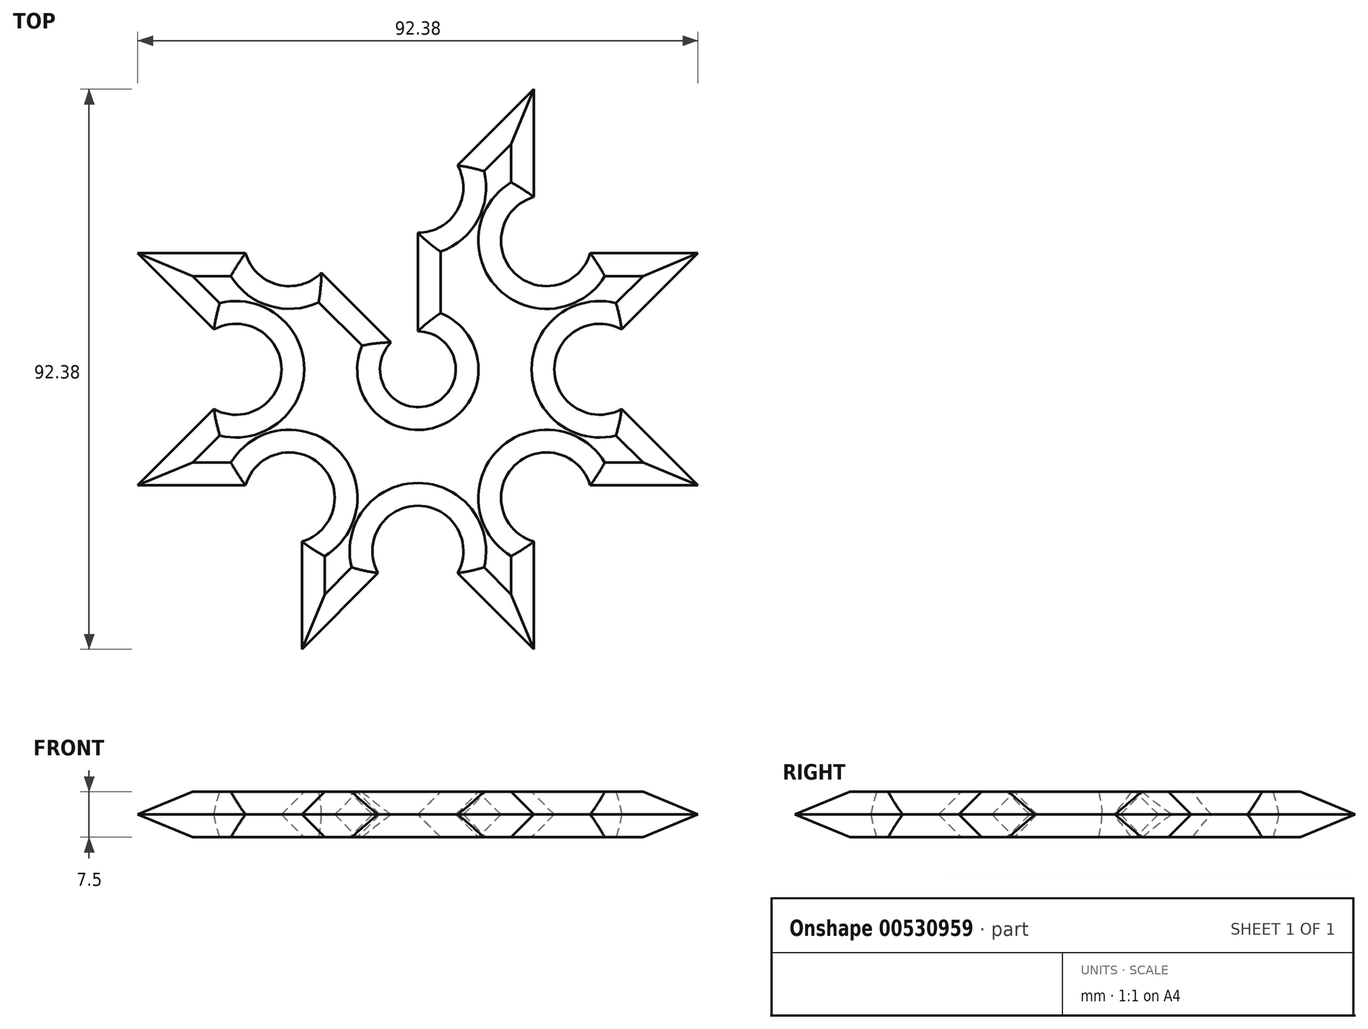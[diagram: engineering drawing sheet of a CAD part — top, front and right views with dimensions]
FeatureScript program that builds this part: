
annotation { "Feature Type Name" : "Feature", "Feature Type Description" : "" }
export const myFeature = defineFeature(function(context is Context, id is Id, definition is map)
    precondition{}
    {
        {
            var Q0;
            Q0=qCreatedBy(makeId("Top.planeOp"),FACE);
            var sketch = newSketch(context, id + "F0", { "sketchPlane" : qUnion([Q0])});
            skCircle(sketch, "E0", {"center": v(0, 0) * mm, "radius": 50 * mm});
            skLineSegment(sketch, "E1", {"start": v(0, 0) * mm, "end": v(0, 50) * mm});
            skLineSegment(sketch, "E2", {"start": v(0, 50) * mm, "end": v(0, 0) * mm});
            skLineSegment(sketch, "E3", {"start": v(0, 0) * mm, "end": v(0, -50) * mm});
            skLineSegment(sketch, "E4", {"start": v(0, -50) * mm, "end": v(0, 0) * mm});
            skLineSegment(sketch, "E5", {"start": v(0, 0) * mm, "end": v(50, 0) * mm});
            skLineSegment(sketch, "E6", {"start": v(0, 0) * mm, "end": v(-50, 0) * mm});
            skLineSegment(sketch, "E7", {"start": v(0, 0) * mm, "end": v(35.36, 35.36) * mm});
            skLineSegment(sketch, "E8", {"start": v(0, 0) * mm, "end": v(-35.36, -35.36) * mm});
            skLineSegment(sketch, "E9", {"start": v(0, 0) * mm, "end": v(-35.36, 35.36) * mm});
            skLineSegment(sketch, "E10", {"start": v(-35.36, 35.36) * mm, "end": v(0, 0) * mm});
            skLineSegment(sketch, "E11", {"start": v(0, 0) * mm, "end": v(35.36, -35.36) * mm});
            skCircle(sketch, "E12", {"center": v(0, 0) * mm, "radius": 6.25 * mm});
            skCircle(sketch, "E13", {"center": v(-21.21, 21.21) * mm, "radius": 7.5 * mm});
            skCircle(sketch, "E14", {"center": v(0, 30) * mm, "radius": 7.5 * mm});
            skCircle(sketch, "E15", {"center": v(21.21, 21.21) * mm, "radius": 7.5 * mm});
            skCircle(sketch, "E16", {"center": v(30, 0) * mm, "radius": 7.5 * mm});
            skCircle(sketch, "E17", {"center": v(21.21, -21.21) * mm, "radius": 7.5 * mm});
            skCircle(sketch, "E18", {"center": v(0, -30) * mm, "radius": 7.5 * mm});
            skCircle(sketch, "E19", {"center": v(-21.21, -21.21) * mm, "radius": 7.5 * mm});
            skCircle(sketch, "E20", {"center": v(-30, 0) * mm, "radius": 7.5 * mm});
            skLineSegment(sketch, "E21", {"start": v(0, 0) * mm, "end": v(-19.13, 46.2) * mm});
            skLineSegment(sketch, "E22", {"start": v(0, 0) * mm, "end": v(19.13, -46.2) * mm});
            skLineSegment(sketch, "E23", {"start": v(0, 0) * mm, "end": v(19.13, 46.2) * mm});
            skLineSegment(sketch, "E24", {"start": v(0, 0) * mm, "end": v(-19.13, -46.2) * mm});
            skLineSegment(sketch, "E25", {"start": v(0, 0) * mm, "end": v(46.2, 19.13) * mm});
            skLineSegment(sketch, "E26", {"start": v(0, 0) * mm, "end": v(46.2, -19.13) * mm});
            skLineSegment(sketch, "E27", {"start": v(0, 0) * mm, "end": v(-46.2, 19.13) * mm});
            skLineSegment(sketch, "E28", {"start": v(0, 0) * mm, "end": v(-46.2, -19.13) * mm});
            skLineSegment(sketch, "E29", {"start": v(-19.13, 46.2) * mm, "end": v(-19.13, 28.42) * mm});
            skLineSegment(sketch, "E30", {"start": v(-19.13, 46.2) * mm, "end": v(-6.57, 33.63) * mm});
            skLineSegment(sketch, "E31", {"start": v(-46.2, 19.13) * mm, "end": v(-33.63, 6.57) * mm});
            skLineSegment(sketch, "E32", {"start": v(-46.2, 19.13) * mm, "end": v(-28.42, 19.13) * mm});
            skLineSegment(sketch, "E33", {"start": v(-33.63, -6.57) * mm, "end": v(-46.2, -19.13) * mm});
            skLineSegment(sketch, "E34", {"start": v(-46.2, -19.13) * mm, "end": v(-28.42, -19.13) * mm});
            skPoint(sketch, "E35.endSnap0", {"position": v(-23.1, -9.57) * mm});
            skLineSegment(sketch, "E36", {"start": v(-19.13, -46.2) * mm, "end": v(-19.13, -46.2) * mm});
            skLineSegment(sketch, "E37", {"start": v(-6.57, -33.63) * mm, "end": v(-19.13, -46.2) * mm});
            skLineSegment(sketch, "E38", {"start": v(-19.13, -46.2) * mm, "end": v(-19.13, -28.42) * mm});
            skLineSegment(sketch, "E39", {"start": v(6.57, -33.63) * mm, "end": v(19.13, -46.2) * mm});
            skLineSegment(sketch, "E40", {"start": v(19.13, -28.42) * mm, "end": v(19.13, -46.2) * mm});
            skLineSegment(sketch, "E41.MirrorCS", {"start": v(19.13, 46.2) * mm, "end": v(6.57, 33.63) * mm});
            skLineSegment(sketch, "E42.MirrorCS", {"start": v(19.13, 28.42) * mm, "end": v(19.13, 46.2) * mm});
            skLineSegment(sketch, "E43.MirrorCS", {"start": v(-6.57, 33.63) * mm, "end": v(-19.13, 46.2) * mm});
            skLineSegment(sketch, "E44.MirrorCS", {"start": v(-19.13, 28.42) * mm, "end": v(-19.13, 46.2) * mm});
            skLineSegment(sketch, "E45.MirrorCS", {"start": v(46.2, -19.13) * mm, "end": v(28.42, -19.13) * mm});
            skLineSegment(sketch, "E46.MirrorCS", {"start": v(46.2, -19.13) * mm, "end": v(33.63, -6.57) * mm});
            skLineSegment(sketch, "E47.MirrorCS", {"start": v(28.42, 19.13) * mm, "end": v(46.2, 19.13) * mm});
            skLineSegment(sketch, "E48.MirrorCS", {"start": v(46.2, 19.13) * mm, "end": v(33.63, 6.57) * mm});
            skSolve(sketch);
        }
        {
            var Q0;
            {var subQ5=sQuery(id+"F0.wireOp",EDGE,"E44.MirrorCS");Q0=makeQuery(id+"F0.imprint","IMPRINT",FACE,{"disambiguationData":[TD([[makeQuery(id+"F0.imprint","IMPRINT",EDGE,{"derivedFrom":subQ5}),-1.0]])]});}
            var Q1;
            {var subQ0=sQuery(id+"F0.wireOp",EDGE,"E43.MirrorCS");Q1=makeQuery(id+"F0.imprint","IMPRINT",FACE,{"disambiguationData":[TD([[makeQuery(id+"F0.imprint","IMPRINT",EDGE,{"derivedFrom":subQ0}),1.0]])]});}
            var Q2;
            {var subQ0=sQuery(id+"F0.wireOp",EDGE,"E41.MirrorCS");Q2=makeQuery(id+"F0.imprint","IMPRINT",FACE,{"disambiguationData":[TD([[makeQuery(id+"F0.imprint","IMPRINT",EDGE,{"derivedFrom":subQ0}),1.0]])]});}
            var Q3;
            {var subQ0=sQuery(id+"F0.wireOp",EDGE,"E42.MirrorCS");Q3=makeQuery(id+"F0.imprint","IMPRINT",FACE,{"disambiguationData":[TD([[makeQuery(id+"F0.imprint","IMPRINT",EDGE,{"derivedFrom":subQ0}),1.0]])]});}
            var Q4;
            {var subQ0=sQuery(id+"F0.wireOp",EDGE,"E47.MirrorCS");Q4=makeQuery(id+"F0.imprint","IMPRINT",FACE,{"disambiguationData":[TD([[makeQuery(id+"F0.imprint","IMPRINT",EDGE,{"derivedFrom":subQ0}),-1.0]])]});}
            var Q5;
            {var subQ0=sQuery(id+"F0.wireOp",EDGE,"E48.MirrorCS");Q5=makeQuery(id+"F0.imprint","IMPRINT",FACE,{"disambiguationData":[TD([[makeQuery(id+"F0.imprint","IMPRINT",EDGE,{"derivedFrom":subQ0}),-1.0]])]});}
            var Q6;
            {var subQ0=sQuery(id+"F0.wireOp",EDGE,"E46.MirrorCS");Q6=makeQuery(id+"F0.imprint","IMPRINT",FACE,{"disambiguationData":[TD([[makeQuery(id+"F0.imprint","IMPRINT",EDGE,{"derivedFrom":subQ0}),1.0]])]});}
            var Q7;
            {var subQ0=sQuery(id+"F0.wireOp",EDGE,"E45.MirrorCS");Q7=makeQuery(id+"F0.imprint","IMPRINT",FACE,{"disambiguationData":[TD([[makeQuery(id+"F0.imprint","IMPRINT",EDGE,{"derivedFrom":subQ0}),-1.0]])]});}
            var Q8;
            {var subQ0=sQuery(id+"F0.wireOp",EDGE,"E40");Q8=makeQuery(id+"F0.imprint","IMPRINT",FACE,{"disambiguationData":[TD([[makeQuery(id+"F0.imprint","IMPRINT",EDGE,{"derivedFrom":subQ0}),-1.0]])]});}
            var Q9;
            {var subQ0=sQuery(id+"F0.wireOp",EDGE,"E39");Q9=makeQuery(id+"F0.imprint","IMPRINT",FACE,{"disambiguationData":[TD([[makeQuery(id+"F0.imprint","IMPRINT",EDGE,{"derivedFrom":subQ0}),1.0]])]});}
            var Q10;
            {var subQ0=sQuery(id+"F0.wireOp",EDGE,"E37");Q10=makeQuery(id+"F0.imprint","IMPRINT",FACE,{"disambiguationData":[TD([[makeQuery(id+"F0.imprint","IMPRINT",EDGE,{"derivedFrom":subQ0}),-1.0]])]});}
            var Q11;
            {var subQ0=sQuery(id+"F0.wireOp",EDGE,"E38");Q11=makeQuery(id+"F0.imprint","IMPRINT",FACE,{"disambiguationData":[TD([[makeQuery(id+"F0.imprint","IMPRINT",EDGE,{"derivedFrom":subQ0}),-1.0]])]});}
            var Q12;
            {var subQ0=sQuery(id+"F0.wireOp",EDGE,"E34");Q12=makeQuery(id+"F0.imprint","IMPRINT",FACE,{"disambiguationData":[TD([[makeQuery(id+"F0.imprint","IMPRINT",EDGE,{"derivedFrom":subQ0}),1.0]])]});}
            var Q13;
            {var subQ0=sQuery(id+"F0.wireOp",EDGE,"E33");Q13=makeQuery(id+"F0.imprint","IMPRINT",FACE,{"disambiguationData":[TD([[makeQuery(id+"F0.imprint","IMPRINT",EDGE,{"derivedFrom":subQ0}),1.0]])]});}
            var Q14;
            {var subQ0=sQuery(id+"F0.wireOp",EDGE,"E31");Q14=makeQuery(id+"F0.imprint","IMPRINT",FACE,{"disambiguationData":[TD([[makeQuery(id+"F0.imprint","IMPRINT",EDGE,{"derivedFrom":subQ0}),1.0]])]});}
            var Q15;
            {var subQ0=sQuery(id+"F0.wireOp",EDGE,"E32");Q15=makeQuery(id+"F0.imprint","IMPRINT",FACE,{"disambiguationData":[TD([[makeQuery(id+"F0.imprint","IMPRINT",EDGE,{"derivedFrom":subQ0}),-1.0]])]});}
            extrude(context, id + "F1", {"entities" : qUnion([Q0, Q1, Q2, Q3, Q4, Q5, Q6, Q7, Q8, Q9, Q10, Q11, Q12, Q13, Q14, Q15]), "depth" : 7.5 * mm, "offsetDistance" : 25 * mm});
        }
        {
            var Q0;
            Q0=makeQuery(id+"F1.opExtrude","CAP_FACE",FACE,{"disambiguationData":[OSD([sQuery(id+"F0.wireOp",EDGE,"E12"),sQuery(id+"F0.wireOp",EDGE,"E13"),sQuery(id+"F0.wireOp",EDGE,"E14"),sQuery(id+"F0.wireOp",EDGE,"E15"),sQuery(id+"F0.wireOp",EDGE,"E16"),sQuery(id+"F0.wireOp",EDGE,"E17"),sQuery(id+"F0.wireOp",EDGE,"E18"),sQuery(id+"F0.wireOp",EDGE,"E19"),sQuery(id+"F0.wireOp",EDGE,"E20"),sQuery(id+"F0.wireOp",EDGE,"E31"),sQuery(id+"F0.wireOp",EDGE,"E32"),sQuery(id+"F0.wireOp",EDGE,"E33"),sQuery(id+"F0.wireOp",EDGE,"E34"),sQuery(id+"F0.wireOp",EDGE,"E37"),sQuery(id+"F0.wireOp",EDGE,"E38"),sQuery(id+"F0.wireOp",EDGE,"E39"),sQuery(id+"F0.wireOp",EDGE,"E40"),sQuery(id+"F0.wireOp",EDGE,"E41.MirrorCS"),sQuery(id+"F0.wireOp",EDGE,"E42.MirrorCS"),sQuery(id+"F0.wireOp",EDGE,"E43.MirrorCS"),sQuery(id+"F0.wireOp",EDGE,"E44.MirrorCS"),sQuery(id+"F0.wireOp",EDGE,"E45.MirrorCS"),sQuery(id+"F0.wireOp",EDGE,"E46.MirrorCS"),sQuery(id+"F0.wireOp",EDGE,"E47.MirrorCS"),sQuery(id+"F0.wireOp",EDGE,"E48.MirrorCS")])],"isStart":true});
            var Q1;
            Q1=makeQuery(id+"F1.opExtrude","CAP_FACE",FACE,{"disambiguationData":[OSD([sQuery(id+"F0.wireOp",EDGE,"E12"),sQuery(id+"F0.wireOp",EDGE,"E13"),sQuery(id+"F0.wireOp",EDGE,"E14"),sQuery(id+"F0.wireOp",EDGE,"E15"),sQuery(id+"F0.wireOp",EDGE,"E16"),sQuery(id+"F0.wireOp",EDGE,"E17"),sQuery(id+"F0.wireOp",EDGE,"E18"),sQuery(id+"F0.wireOp",EDGE,"E19"),sQuery(id+"F0.wireOp",EDGE,"E20"),sQuery(id+"F0.wireOp",EDGE,"E31"),sQuery(id+"F0.wireOp",EDGE,"E32"),sQuery(id+"F0.wireOp",EDGE,"E33"),sQuery(id+"F0.wireOp",EDGE,"E34"),sQuery(id+"F0.wireOp",EDGE,"E37"),sQuery(id+"F0.wireOp",EDGE,"E38"),sQuery(id+"F0.wireOp",EDGE,"E39"),sQuery(id+"F0.wireOp",EDGE,"E40"),sQuery(id+"F0.wireOp",EDGE,"E41.MirrorCS"),sQuery(id+"F0.wireOp",EDGE,"E42.MirrorCS"),sQuery(id+"F0.wireOp",EDGE,"E43.MirrorCS"),sQuery(id+"F0.wireOp",EDGE,"E44.MirrorCS"),sQuery(id+"F0.wireOp",EDGE,"E45.MirrorCS"),sQuery(id+"F0.wireOp",EDGE,"E46.MirrorCS"),sQuery(id+"F0.wireOp",EDGE,"E47.MirrorCS"),sQuery(id+"F0.wireOp",EDGE,"E48.MirrorCS")])],"isStart":false});
            chamfer(context, id + "F2", {"entities" : qUnion([Q0, Q1]), "width" : 3.75 * mm, "tangentPropagation" : true});
        }
    });
